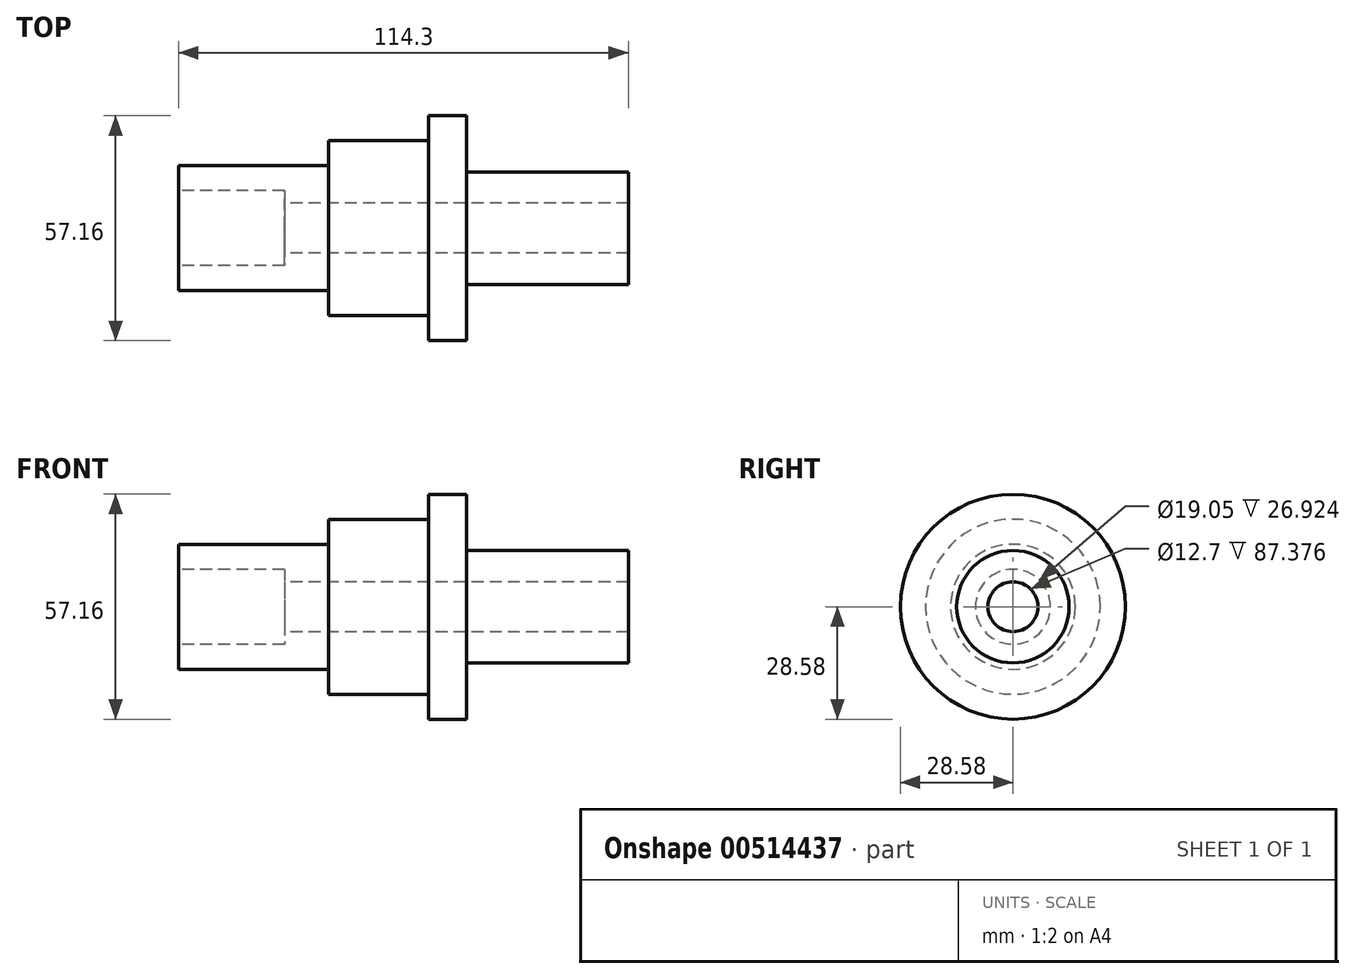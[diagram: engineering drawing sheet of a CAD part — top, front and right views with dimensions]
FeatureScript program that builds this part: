
annotation { "Feature Type Name" : "Feature", "Feature Type Description" : "" }
export const myFeature = defineFeature(function(context is Context, id is Id, definition is map)
    precondition{}
    {
        {
            var Q0;
            Q0=qCreatedBy(makeId("Front.planeOp"),FACE);
            var sketch = newSketch(context, id + "F0", { "sketchPlane" : qUnion([Q0])});
            skLineSegment(sketch, "E0", {"start": v(-42.3, 0) * mm, "end": v(42.3, 0) * mm, "construction": true});
            skPoint(sketch, "E1", {"position": v(0, 0) * mm});
            skLineSegment(sketch, "E2", {"start": v(-73.15, 9.53) * mm, "end": v(-73.15, 15.88) * mm});
            skLineSegment(sketch, "E3", {"start": v(-73.15, 15.88) * mm, "end": v(-35.05, 15.88) * mm});
            skLineSegment(sketch, "E4", {"start": v(-35.05, 15.88) * mm, "end": v(-35.05, 22.23) * mm});
            skLineSegment(sketch, "E5", {"start": v(-35.05, 22.23) * mm, "end": v(-9.65, 22.23) * mm});
            skLineSegment(sketch, "E6", {"start": v(-9.65, 22.23) * mm, "end": v(-9.65, 28.58) * mm});
            skLineSegment(sketch, "E7", {"start": v(-9.65, 28.58) * mm, "end": v(0, 28.58) * mm});
            skLineSegment(sketch, "E8", {"start": v(0, 28.58) * mm, "end": v(0, 14.29) * mm});
            skLineSegment(sketch, "E9", {"start": v(0, 14.29) * mm, "end": v(41.15, 14.29) * mm});
            skLineSegment(sketch, "E10", {"start": v(41.15, 14.29) * mm, "end": v(41.15, 6.35) * mm});
            skLineSegment(sketch, "E11", {"start": v(41.15, 6.35) * mm, "end": v(-46.23, 6.35) * mm});
            skLineSegment(sketch, "E12", {"start": v(-46.23, 6.35) * mm, "end": v(-46.23, 9.53) * mm});
            skLineSegment(sketch, "E13", {"start": v(-46.23, 9.53) * mm, "end": v(-73.15, 9.53) * mm});
            skSolve(sketch);
        }
        {
            var Q0;
            Q0=makeQuery(id+"F0.imprint","IMPRINT",FACE,{"disambiguationData":[TD([[makeQuery(id+"F0.imprint","IMPRINT",EDGE,{"derivedFrom":sQuery(id+"F0.wireOp",EDGE,"E2")}),-1.0]])]});
            var Q1;
            Q1=sQuery(id+"F0.wireOp",EDGE,"E0");
            revolve(context, id + "F1", {"entities" : qUnion([Q0]), "axis" : qUnion([Q1]), "revolveType" : RevolveType.FULL});
        }
    });
